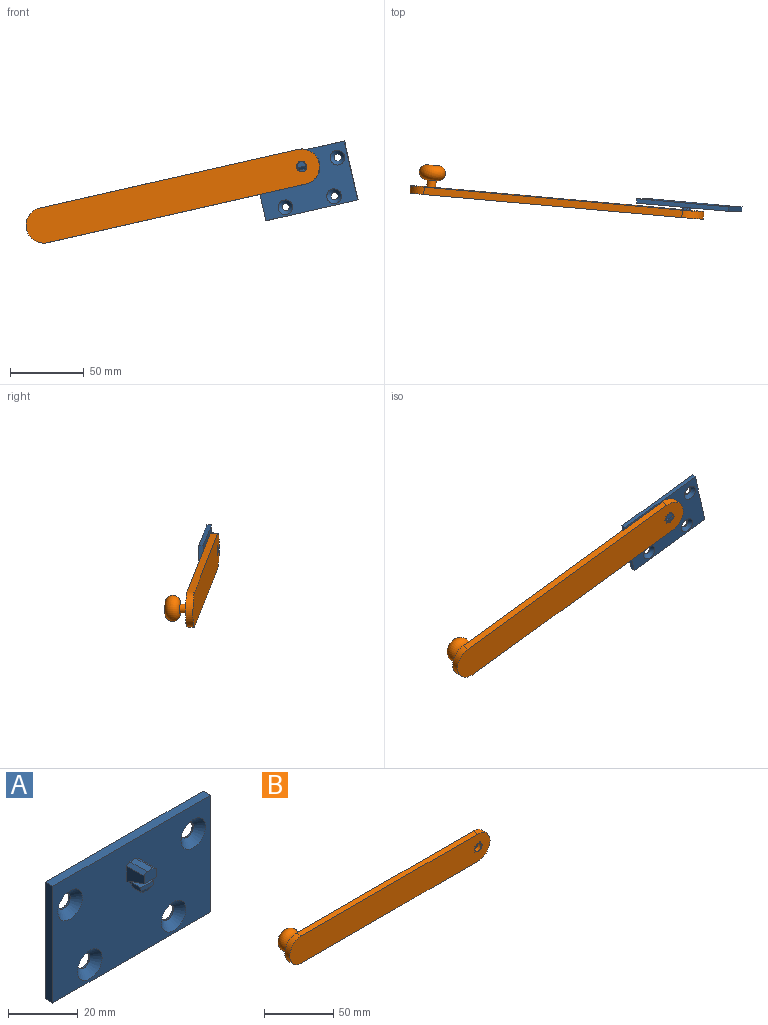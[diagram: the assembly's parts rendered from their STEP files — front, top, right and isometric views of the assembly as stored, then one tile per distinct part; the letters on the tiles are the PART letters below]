
ASSEMBLY  parts=2 mates=1
PART A: 31 faces, bbox 64x10x41 mm
  f0: plane 5x4.73mm, normal (0,0,1), area 23.6mm2, adj f1,f2,f29,f30
  f1: plane 7x6.33mm, normal (-1,0,0), area 34.3mm2, adj f0,f3,f4,f18,f22,f23,f24,f29
  f2: plane 7x6.33mm, normal (1,0,0), area 34.3mm2, adj f0,f3,f4,f19,f22,f26,f27,f29
  f3: plane 5x3.66mm, normal (0,-1,0), area 17.2mm2, adj f1,f2,f23,f27,f28,f29
  f4: plane 64x41mm, normal (0,-1,0), area 2277mm2, adj f1,f2,f5,f6,f7,f8,f11,f13
  f5: plane 64x3mm, normal (0,0,1), area 192mm2, adj f4,f6,f8,f9
  f6: plane 41x3mm, normal (-1,0,0), area 123mm2, adj f4,f5,f7,f9
  f7: plane 64x3mm, normal (0,0,-1), area 192mm2, adj f4,f6,f8,f9
  f8: plane 41x3mm, normal (1,0,0), area 123mm2, adj f4,f5,f7,f9
  f9: plane 64x41mm, normal (0,1,0), area 2545.5mm2, adj f5,f6,f7,f8,f10,f12,f14,f16
  f10: cylinder r=2.5mm len=5mm, axis (0,-1,0), area 7.9mm2, adj f9,f11
  f11: cone r=2.5mm half-angle=45deg, axis (0,-1,0), area 83.3mm2, adj f4,f10
  f12: cylinder r=2.5mm len=5mm, axis (0,-1,0), area 7.9mm2, adj f9,f13
  f13: cone r=2.5mm half-angle=45deg, axis (0,-1,0), area 83.3mm2, adj f4,f12
  f14: cylinder r=2.5mm len=5mm, axis (0,-1,0), area 7.9mm2, adj f9,f15
  f15: cone r=2.5mm half-angle=45deg, axis (0,-1,0), area 83.3mm2, adj f4,f14
  f16: cylinder r=2.5mm len=5mm, axis (0,-1,0), area 7.9mm2, adj f9,f17
  f17: cone r=2.5mm half-angle=45deg, axis (0,-1,0), area 83.3mm2, adj f4,f16
  f18: plane 3.46x1.29mm, normal (-0.54,0,-0.84), area 5mm2, adj f1,f20,f21,f22
  f19: plane 3.46x1.29mm, normal (0.54,0,-0.84), area 5mm2, adj f2,f20,f21,f22
  f20: plane 3x2.43mm, normal (0,0,-1), area 7.3mm2, adj f18,f19,f21,f22
  f21: plane 5x0.84mm, normal (0,-0.96,-0.26), area 3.2mm2, adj f18,f19,f20,f30
  f22: plane 5x1.84mm, normal (0,0.96,-0.26), area 5.2mm2, adj f1,f2,f18,f19,f20,f24,f25,f26
  f23: plane 7x1.29mm, normal (-0.54,0,0.84), area 10.7mm2, adj f1,f3,f4,f28
  f24: plane 2.23x1.29mm, normal (-0.54,0,-0.84), area 3.2mm2, adj f1,f4,f22,f25
  f25: plane 2.43x2.23mm, normal (0,0,-1), area 5.4mm2, adj f4,f22,f24,f26
  f26: plane 2.23x1.29mm, normal (0.54,0,-0.84), area 3.2mm2, adj f2,f4,f22,f25
  f27: plane 7x1.29mm, normal (0.54,0,0.84), area 10.7mm2, adj f2,f3,f4,f28
  f28: plane 7x2.43mm, normal (0,0,1), area 17mm2, adj f3,f4,f23,f27
  f29: plane 6x5mm, normal (0,-0.32,-0.95), area 31.6mm2, adj f0,f1,f2,f3
  f30: plane 5x1.5mm, normal (0,-1,0), area 7.5mm2, adj f0,f1,f2,f21
PART B: 15 faces, bbox 204x20x24 mm
  f0: cylinder r=12mm len=24mm, axis (0,1,0), area 188.5mm2, adj f1,f3,f4,f5
  f1: plane 180x5mm, normal (0,0,-1), area 900mm2, adj f0,f2,f4,f5
  f2: cylinder r=12mm len=24mm, axis (0,1,0), area 188.5mm2, adj f1,f3,f4,f5
  f3: plane 180x5mm, normal (0,0,1), area 900mm2, adj f0,f2,f4,f5
  f4: plane 204x24mm, normal (0,-1,0), area 4733.9mm2, adj f0,f1,f2,f3,f14
  f5: plane 204x24mm, normal (0,1,0), area 4705.6mm2, adj f0,f1,f2,f3,f6,f10
  f6: cylinder r=3mm len=6mm, axis (0,1,0), area 94.2mm2, adj f5,f7
  f7: plane 7.67x7.67mm, normal (0,-1,0), area 17.9mm2, adj f6,f8
  f8: torus R=3.83mm, axis (0,1,0), area 692.6mm2, adj f7,f9
  f9: plane 7.67x7.67mm, normal (0,1,0), area 46.2mm2, adj f8
  f10: cylinder r=3.5mm len=7mm, axis (0,-1,0), area 11mm2, adj f5,f11
  f11: plane 9x9mm, normal (0,-1,0), area 25.1mm2, adj f10,f12
  f12: cylinder r=4.5mm len=9mm, axis (0,-1,0), area 113.1mm2, adj f11,f13
  f13: plane 9x9mm, normal (0,1,0), area 25.1mm2, adj f12,f14
  f14: cylinder r=3.5mm len=7mm, axis (0,-1,0), area 11mm2, adj f4,f13
PLACE A rot(axis=(0.04,-0.93,-0.36),13.7deg) t=(90.65,-19.9,-32.3)mm
PLACE B rot(axis=(0.04,-0.93,-0.36),13.7deg) t=(-43.16,-12.97,-59.82)mm
MATE revolute B.f2 <-> A.f3  axis (-0.08,-1,-0.02) through (43.84,-25.8,-40.05)mm
